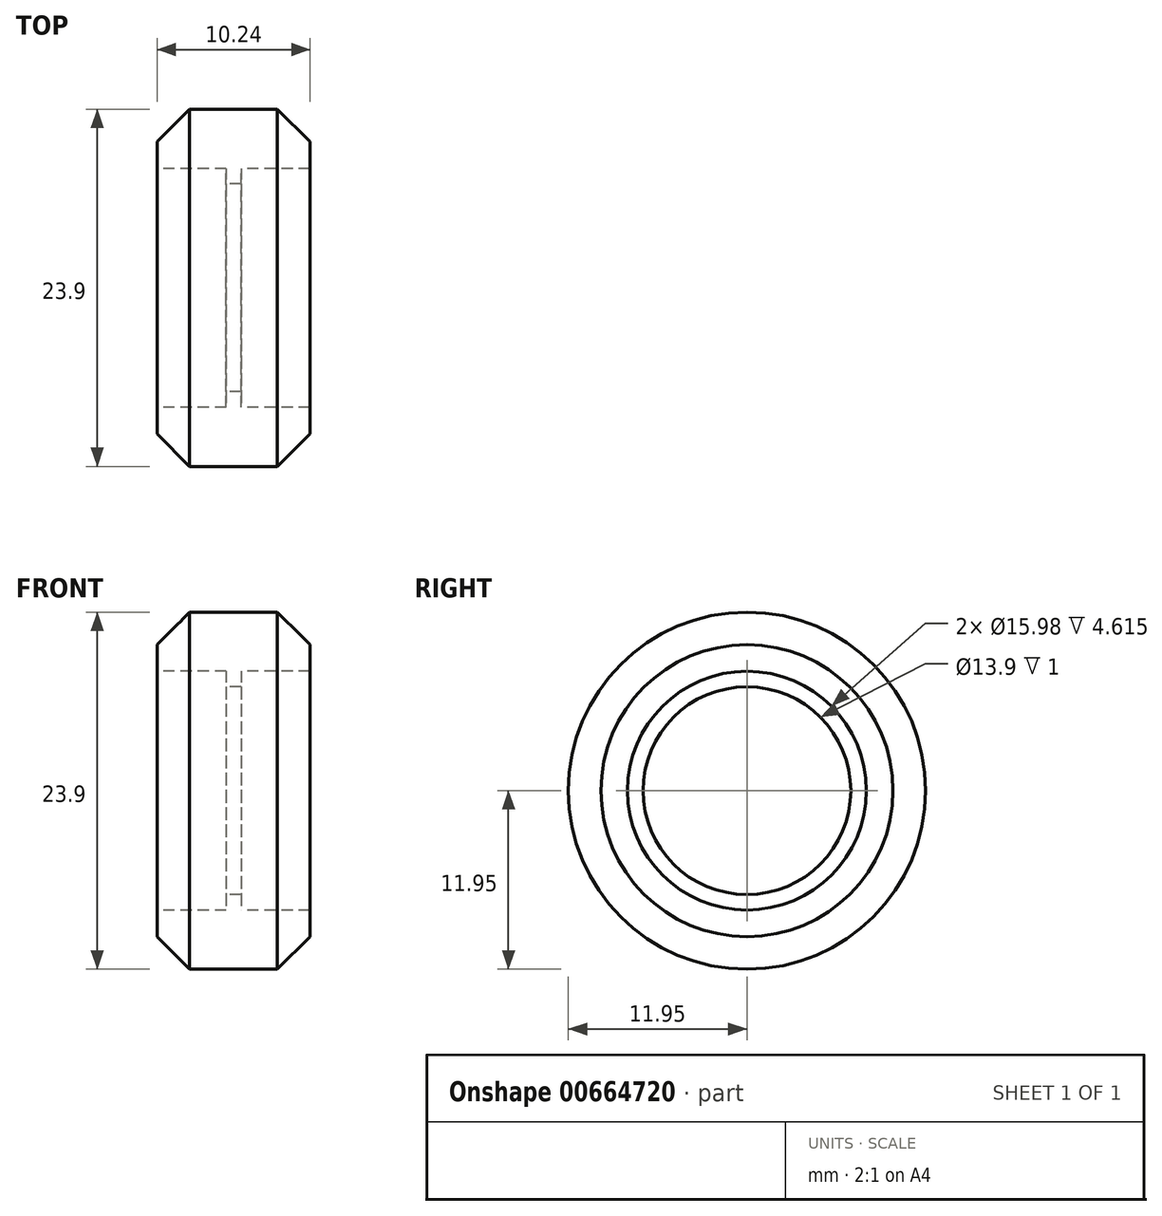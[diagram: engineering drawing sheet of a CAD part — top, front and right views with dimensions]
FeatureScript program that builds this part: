
annotation { "Feature Type Name" : "Feature", "Feature Type Description" : "" }
export const myFeature = defineFeature(function(context is Context, id is Id, definition is map)
    precondition{}
    {
        {
            var Q0;
            Q0=qCreatedBy(makeId("Front.planeOp"),FACE);
            var sketch = newSketch(context, id + "F0", { "sketchPlane" : qUnion([Q0])});
            skLineSegment(sketch, "E0", {"start": v(-37.53, 0) * mm, "end": v(39.43, 0) * mm, "construction": true});
            skLineSegment(sketch, "E1.0", {"start": v(-37.53, 6.95) * mm, "end": v(39.43, 6.95) * mm, "construction": true});
            skLineSegment(sketch, "E2.0", {"start": v(-37.53, 8) * mm, "end": v(39.43, 8) * mm, "construction": true});
            skLineSegment(sketch, "E3.0", {"start": v(-37.53, 9.77) * mm, "end": v(39.43, 9.77) * mm, "construction": true});
            skLineSegment(sketch, "E4.0", {"start": v(-37.53, 11.95) * mm, "end": v(39.43, 11.95) * mm, "construction": true});
            skLineSegment(sketch, "E5", {"start": v(0, 0.24) * mm, "end": v(0, 13.06) * mm, "construction": true});
            skLineSegment(sketch, "E6.0", {"start": v(5.11, 0.24) * mm, "end": v(5.11, 13.06) * mm, "construction": true});
            skLineSegment(sketch, "E7.0", {"start": v(-5.12, 0.24) * mm, "end": v(-5.12, 13.06) * mm, "construction": true});
            skLineSegment(sketch, "E8", {"start": v(-5.12, 9.77) * mm, "end": v(-1.72, 13.16) * mm, "construction": true});
            skLineSegment(sketch, "E9", {"start": v(5.12, 9.77) * mm, "end": v(2.14, 12.75) * mm, "construction": true});
            skLineSegment(sketch, "E10.0", {"start": v(0.5, 0.24) * mm, "end": v(0.5, 13.06) * mm, "construction": true});
            skLineSegment(sketch, "E11.0", {"start": v(-0.5, 0.24) * mm, "end": v(-0.5, 13.06) * mm, "construction": true});
            skLineSegment(sketch, "E12", {"start": v(-0.5, 6.95) * mm, "end": v(-0.5, 8) * mm});
            skLineSegment(sketch, "E13", {"start": v(-0.5, 8) * mm, "end": v(-5.12, 8) * mm});
            skLineSegment(sketch, "E14", {"start": v(-5.12, 8) * mm, "end": v(-5.12, 9.77) * mm});
            skLineSegment(sketch, "E15", {"start": v(-5.12, 9.77) * mm, "end": v(-2.94, 11.95) * mm});
            skLineSegment(sketch, "E16", {"start": v(-2.94, 11.95) * mm, "end": v(2.94, 11.95) * mm});
            skLineSegment(sketch, "E17", {"start": v(2.93, 11.95) * mm, "end": v(5.12, 9.77) * mm});
            skLineSegment(sketch, "E18", {"start": v(5.12, 9.77) * mm, "end": v(5.12, 8) * mm});
            skLineSegment(sketch, "E19", {"start": v(5.12, 8) * mm, "end": v(0.5, 8) * mm});
            skLineSegment(sketch, "E20", {"start": v(0.5, 8) * mm, "end": v(0.5, 6.95) * mm});
            skLineSegment(sketch, "E21", {"start": v(0.5, 6.95) * mm, "end": v(-0.5, 6.95) * mm});
            skSolve(sketch);
        }
        {
            var Q0;
            Q0 = qSketchRegion(id + "F0", true);
            var Q1;
            Q1=sQuery(id+"F0.wireOp",EDGE,"E0");
            revolve(context, id + "F1", {"entities" : qUnion([Q0]), "axis" : qUnion([Q1]), "revolveType" : RevolveType.FULL});
        }
    });
